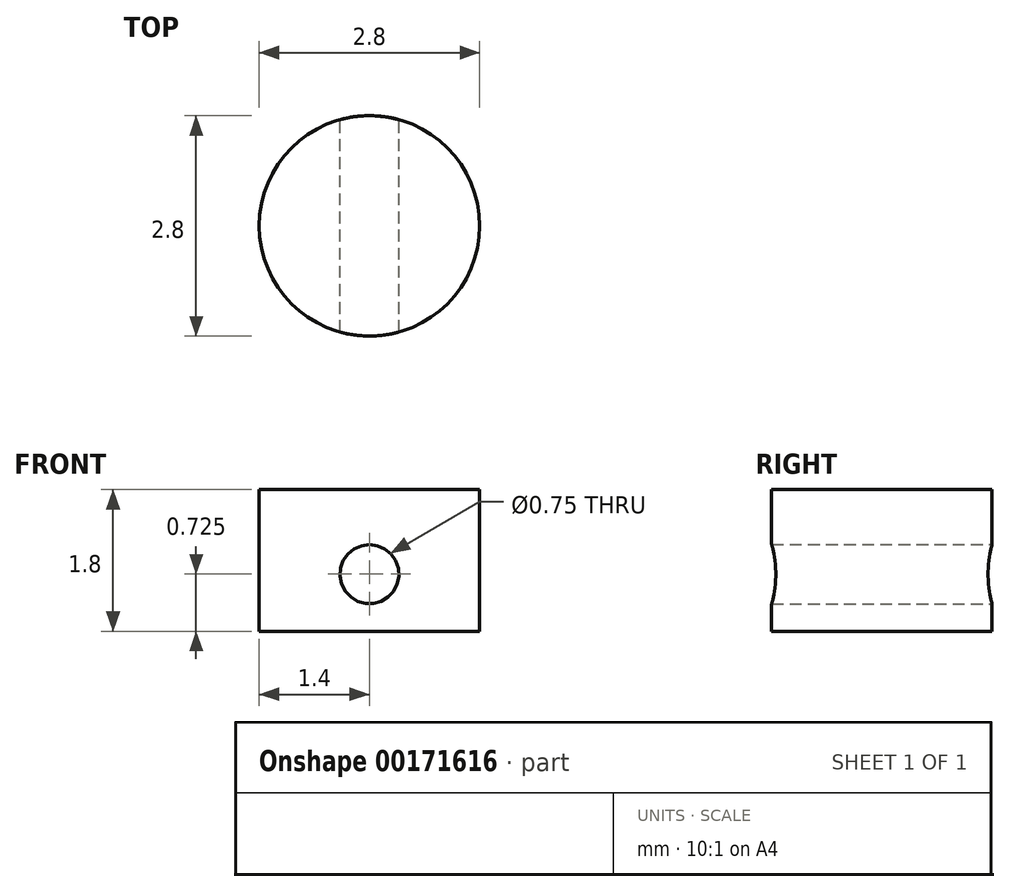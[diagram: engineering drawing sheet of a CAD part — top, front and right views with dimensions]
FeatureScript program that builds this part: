
annotation { "Feature Type Name" : "Feature", "Feature Type Description" : "" }
export const myFeature = defineFeature(function(context is Context, id is Id, definition is map)
    precondition{}
    {
        {
            var Q0;
            Q0=qCreatedBy(makeId("Top.planeOp"),FACE);
            var sketch = newSketch(context, id + "F0", { "sketchPlane" : qUnion([Q0])});
            skCircle(sketch, "E0", {"center": v(0, 0) * mm, "radius": 1.4 * mm});
            skSolve(sketch);
        }
        {
            var Q0;
            Q0 = qSketchRegion(id + "F0", true);
            extrude(context, id + "F1", {"entities" : qUnion([Q0]), "depth" : 1.8 * mm});
        }
        {
            var Q0;
            Q0=qCreatedBy(makeId("Front.planeOp"),FACE);
            var sketch = newSketch(context, id + "F2", { "sketchPlane" : qUnion([Q0])});
            skCircle(sketch, "E1", {"center": v(0, 0.72) * mm, "radius": 0.38 * mm});
            skSolve(sketch);
        }
        {
            var Q0;
            Q0 = qSketchRegion(id + "F2", true);
            var Q1;
            Q1=sQuery(id+"F2.wireOp",EDGE,"E1");
            extrude(context, id + "F3", {"entities" : qUnion([Q0]), "operationType" : NewBodyOperationType.REMOVE, "surfaceEntities" : qUnion([Q1]), "depth" : 25 * mm, "symmetric" : true});
        }
    });
